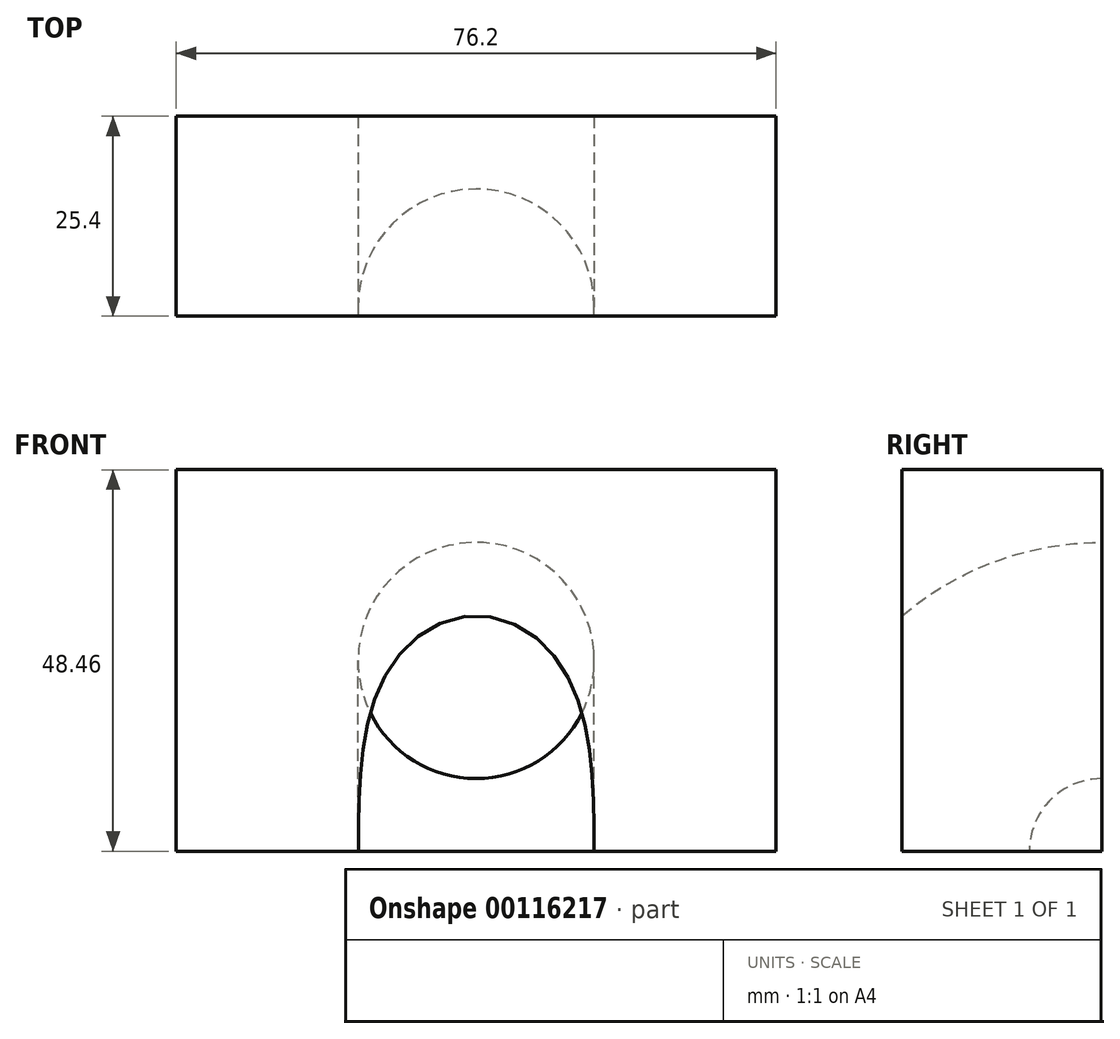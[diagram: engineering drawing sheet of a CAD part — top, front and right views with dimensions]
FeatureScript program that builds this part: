
annotation { "Feature Type Name" : "Feature", "Feature Type Description" : "" }
export const myFeature = defineFeature(function(context is Context, id is Id, definition is map)
    precondition{}
    {
        {
            var Q0;
            Q0=qCreatedBy(makeId("Front.planeOp"),FACE);
            var sketch = newSketch(context, id + "F0", { "sketchPlane" : qUnion([Q0])});
            skLineSegment(sketch, "E0.bottom", {"start": v(38.1, -24.23) * mm, "end": v(-38.1, -24.23) * mm});
            skLineSegment(sketch, "E0.top", {"start": v(38.1, 24.23) * mm, "end": v(-38.1, 24.23) * mm});
            skLineSegment(sketch, "E0.left", {"start": v(38.1, -24.23) * mm, "end": v(38.1, 24.23) * mm});
            skLineSegment(sketch, "E0.right", {"start": v(-38.1, -24.23) * mm, "end": v(-38.1, 24.23) * mm});
            skPoint(sketch, "E0.middle", {"position": v(0, 0) * mm});
            skSolve(sketch);
        }
        {
            var Q0;
            Q0 = qSketchRegion(id + "F0", true);
            extrude(context, id + "F1", {"entities" : qUnion([Q0]), "depth" : 25.4 * mm});
        }
        {
            var Q0;
            Q0=makeQuery(id+"F0.imprint","IMPRINT",FACE,{"disambiguationData":[TD([[makeQuery(id+"F0.imprint","IMPRINT",EDGE,{"derivedFrom":sQuery(id+"F0.wireOp",EDGE,"E0.bottom")}),-1.0]])]});
            var sketch = newSketch(context, id + "F2", { "sketchPlane" : qUnion([Q0])});
            skCircle(sketch, "E1", {"center": v(0, 0) * mm, "radius": 15 * mm});
            skSolve(sketch);
        }
        {
            var Q0;
            Q0 = qSketchRegion(id + "F2", true);
            var Q1;
            Q1=sQuery(id+"F0.wireOp",EDGE,"E0.bottom");
            revolve(context, id + "F3", {"operationType" : NewBodyOperationType.REMOVE, "entities" : qUnion([Q0]), "axis" : qUnion([Q1]), "revolveType" : RevolveType.FULL});
        }
    });
